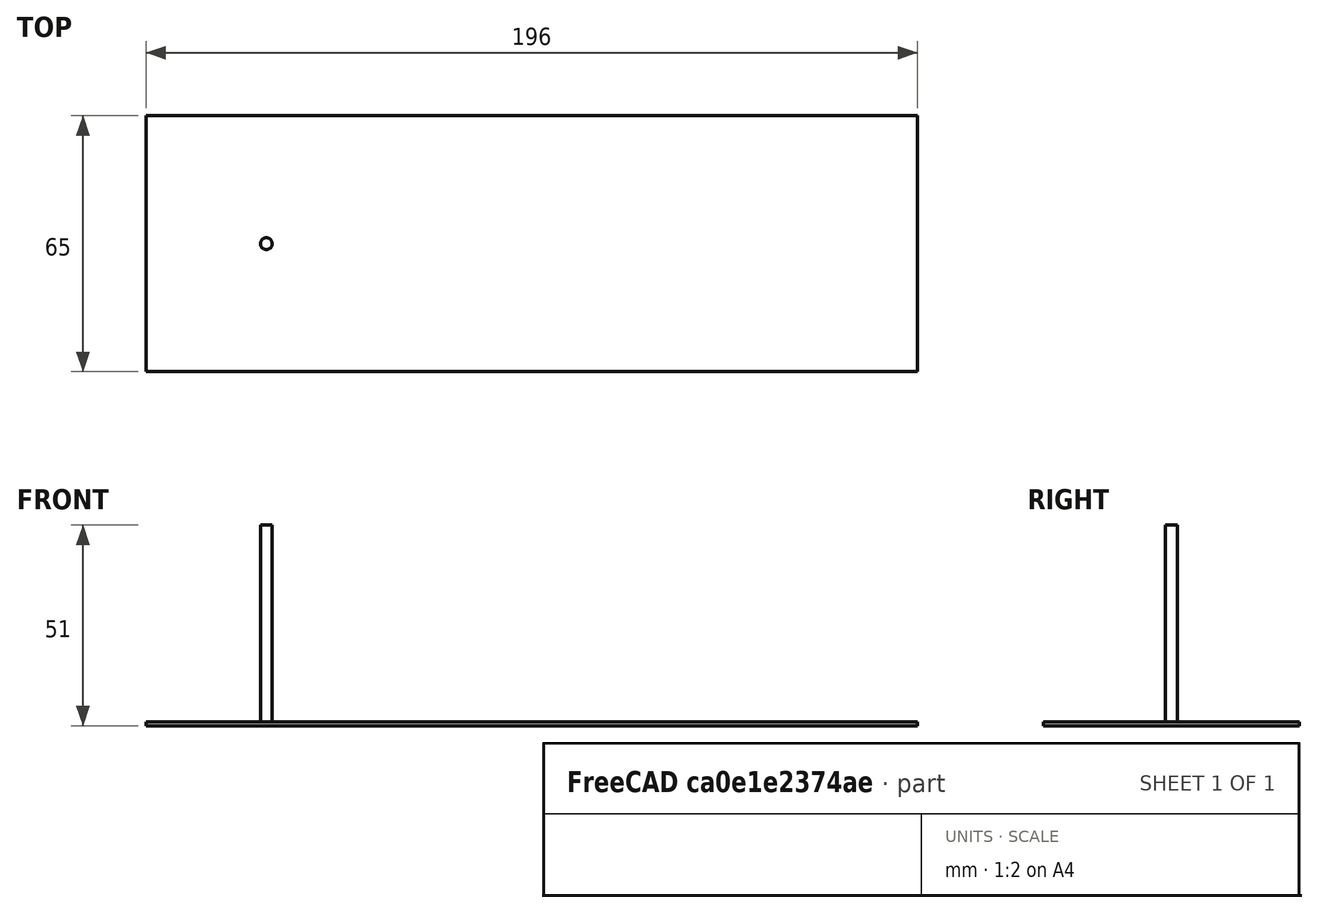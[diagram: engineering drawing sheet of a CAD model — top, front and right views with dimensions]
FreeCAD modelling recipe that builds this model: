
FCSTD DOCUMENT  (FreeCAD 1.0R39319 (Git))
Label: BackPanel
License: All rights reserved
LicenseURL: https://en.wikipedia.org/wiki/All_rights_reserved
objects: Part::FeaturePython×3, App::DocumentObjectGroup×3, Path::FeaturePython×3, Part::Feature×1, PartDesign::FeatureBase×1, PartDesign::Body×1, App::FeaturePython×1
note: 8 computed .brp shape members not serialized (recipe doc carries the construction recipe); baked Part::Feature solids carry a one-line shape summary decoded from their .brp

FEATURE [Part::Feature] Part__Feature  label="ААНЗ.741138.155"
  shape: bbox 194 x 63 x 1 mm, 62 faces (baked)
FEATURE [PartDesign::FeatureBase] BaseFeature
  BaseFeature = -> Part__Feature
  Suppressed = false
FEATURE [PartDesign::Body] Body
  AllowCompound = false
  BaseFeature = -> Part__Feature
  Group = -> [BaseFeature]
  Origin = -> Origin
  Tip = -> BaseFeature
FEATURE [App::FeaturePython] SetupSheet  # Path/CAM operation (typed FeaturePython)
  ClearanceHeightExpression = OpStockZMax+SetupSheet.ClearanceHeightOffset
  ClearanceHeightOffset = 5
  CoolantMode = 0
  CoolantModes = None | Flood | Mist
  FinalDepthExpression = OpFinalDepth
  HorizRapid = 0
  SafeHeightExpression = OpStockZMax+SetupSheet.SafeHeightOffset
  SafeHeightOffset = 3
  StartDepthExpression = OpStartDepth
  StepDownExpression = OpToolDiameter
  VertRapid = 0
FEATURE [Part::FeaturePython] Clone  label="Model-Body"  # Draft clone (typed FeaturePython)
  AttacherType = Attacher::AttachEngine3D
  Fuse = false
  Objects = -> [Body]
  PathResource = Model
  Placement = pos=(67.4,0,-1) rot=(0,0,1;0rad)
  Scale = (1,1,1)
FEATURE [App::DocumentObjectGroup] Model
  Group = -> [Clone]
FEATURE [Part::FeaturePython] Stock  # WARN: FeaturePython — macro-defined, semantics opaque (R4)
  Base = -> Model
  ExtXneg = 1
  ExtXpos = 1
  ExtYneg = 1
  ExtYpos = 1
  ExtZneg = 0
  ExtZpos = 0
  Placement = pos=(-29.6,-31.5,-1) rot=(0,0,1;0rad)
  StockType = FromBase
FEATURE [Part::FeaturePython] ToolBit001  label="3mm Endmill"  # Path/CAM toolbit (typed FeaturePython)
  BitPropertyNames = Chipload | CuttingEdgeHeight | Diameter | Flutes | Length | Material | ShankDiameter | SpindleDirection
  BitShape = C:/Program Files/FreeCAD 1.0/Mod/CAM/Tools\Shape\endmill.fcstd
  Chipload = 0
  CuttingEdgeHeight = 30
  Diameter = 3
  File = C:/Program Files/FreeCAD 1.0/Mod/CAM/Tools/Bit/3mm_Endmill.fctb
  Flutes = 0
  Length = 50
  Material = 0
  ShankDiameter = 3
  ShapeName = endmill
  SpindleDirection = 0
FEATURE [Path::FeaturePython] _mm_Endmill  label="3mm Endmill001"  # Path/CAM operation (typed FeaturePython)
  HorizFeed = 6.66667
  HorizRapid = 0
  SpindleDir = 0
  SpindleSpeed = 10000
  Tool = -> ToolBit001
  ToolNumber = 2
  VertFeed = 6.66667
  VertRapid = 0
  expr: HorizRapid = SetupSheet.HorizRapid
  expr: VertRapid = SetupSheet.VertRapid
FEATURE [App::DocumentObjectGroup] Tools
  Group = -> [_mm_Endmill]
FEATURE [Path::FeaturePython] Profile  # Path/CAM operation (typed FeaturePython)
  Active = true
  AreaParams:
    Tolerance = 1e-07
    FitArcs = True
    Simplify = False
    CleanDistance = 0.0
    Accuracy = 0.01
    Unit = 1.0
    MinArcPoints = 4
    MaxArcPoints = 100
    ClipperScale = 10000000.0
    Fill = 0
    Coplanar = 0
    Reorient = True
    Outline = False
    Explode = False
    OpenMode = 0
    Deflection = 0.01
    SubjectFill = 0
    ClipFill = 0
    Offset = -1.5
    ExtraPass = 0
    Stepover = 0.0
    LastStepover = 0.0
    JoinType = 0
    EndType = 0
    MiterLimit = 2.0
    RoundPrecision = 0.0
    PocketMode = 0
    ToolRadius = 1.0
    PocketExtraOffset = 0.0
    PocketStepover = 0.0
    PocketLastStepover = 0.0
    FromCenter = False
    Angle = 45.0
    AngleShift = 0.0
    Shift = 0.0
    Thicken = False
    SectionCount = -1
    Stepdown = 1.0
    SectionOffset = 0.0
    SectionTolerance = 1e-06
    SectionMode = 2
    Project = False
  Base = -> [Clone]
  ClearanceHeight = 5
  CoolantMode = 0
  CycleTime = 00:00:54
  Direction = 0
  FinalDepth = -1
  HandleMultipleFeatures = 0
  JoinType = 0
  MiterLimit = 0.1
  OffsetExtra = 0
  OpFinalDepth = -1
  OpStartDepth = 9e-16
  OpStockZMax = 9e-16
  OpStockZMin = -1
  OpToolDiameter = 3
  PathParams:
    orientation = 1
    feedrate = 6.666666666666667
    feedrate_v = 6.666666666666667
    verbose = True
    resume_height = 3.000000000000001
    retraction = 5.000000000000001
    return_end = True
    preamble = False
  SafeHeight = 3
  Side = 1
  SplitArcs = false
  StartDepth = 9e-16
  StartPoint = (0,0,0)
  StepDown = 0.3
  ToolController = -> _mm_Endmill
  UseComp = true
  UseStartPoint = false
  processCircles = false
  processHoles = false
  processPerimeter = true
  expr: ClearanceHeight = OpStockZMax + SetupSheet.ClearanceHeightOffset
  expr: FinalDepth = OpFinalDepth
  expr: SafeHeight = OpStockZMax + SetupSheet.SafeHeightOffset
  expr: StartDepth = OpStartDepth
  expr: StepDown = OpToolDiameter / 10
FEATURE [App::DocumentObjectGroup] Operations
  Group = -> [Profile]
FEATURE [Path::FeaturePython] Job  # Path/CAM operation (typed FeaturePython)
  CycleTime = 00:00:54
  Fixtures = G54
  GeometryTolerance = 0.01
  JobType = 0
  Model = -> Model
  Operations = -> Operations
  OrderOutputBy = 0
  PostProcessor = 11
  PostProcessorArgs = --bcnc
  PostProcessorOutputFile = %D/%d
  SetupSheet = -> SetupSheet
  SplitOutput = false
  Stock = -> Stock
  Tools = -> Tools
